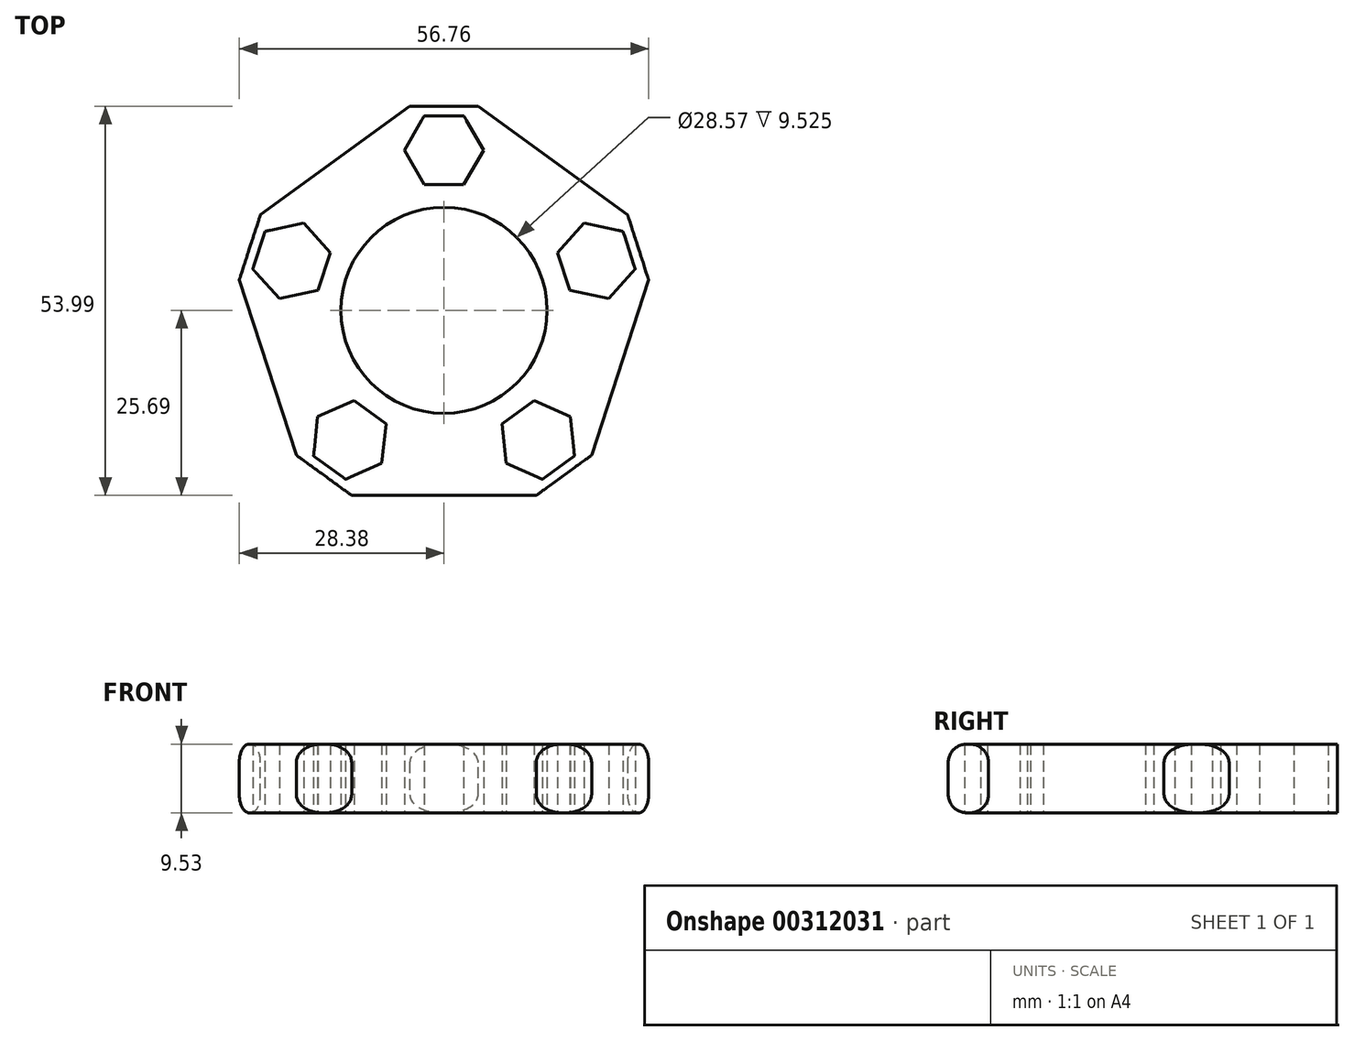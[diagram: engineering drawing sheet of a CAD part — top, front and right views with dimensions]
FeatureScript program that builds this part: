
annotation { "Feature Type Name" : "Feature", "Feature Type Description" : "" }
export const myFeature = defineFeature(function(context is Context, id is Id, definition is map)
    precondition{}
    {
        {
            var Q0;
            Q0=qCreatedBy(makeId("Top.planeOp"),FACE);
            var sketch = newSketch(context, id + "F0", { "sketchPlane" : qUnion([Q0])});
            skCircle(sketch, "E0", {"center": v(0, 0) * mm, "radius": 14.29 * mm});
            skLineSegment(sketch, "E1.0", {"start": v(-2.75, 26.99) * mm, "end": v(2.75, 26.99) * mm});
            skLineSegment(sketch, "E1.1", {"start": v(2.75, 26.99) * mm, "end": v(5.5, 22.23) * mm});
            skLineSegment(sketch, "E1.2", {"start": v(5.5, 22.23) * mm, "end": v(2.75, 17.46) * mm});
            skLineSegment(sketch, "E1.3", {"start": v(2.75, 17.46) * mm, "end": v(-2.75, 17.46) * mm});
            skLineSegment(sketch, "E1.4", {"start": v(-2.75, 17.46) * mm, "end": v(-5.5, 22.22) * mm});
            skLineSegment(sketch, "E1.5", {"start": v(-5.5, 22.22) * mm, "end": v(-2.75, 26.99) * mm});
            skPoint(sketch, "E1.0.midPoint", {"position": v(0, 26.99) * mm});
            skLineSegment(sketch, "E2.1.0", {"start": v(-19.44, 12.1) * mm, "end": v(-15.76, 8.01) * mm});
            skLineSegment(sketch, "E2.1.1", {"start": v(-17.46, 2.78) * mm, "end": v(-22.84, 1.64) * mm});
            skLineSegment(sketch, "E2.1.2", {"start": v(-15.76, 8.01) * mm, "end": v(-17.46, 2.78) * mm});
            skLineSegment(sketch, "E2.1.3", {"start": v(-22.84, 1.64) * mm, "end": v(-26.52, 5.72) * mm});
            skLineSegment(sketch, "E2.1.4", {"start": v(-24.82, 10.95) * mm, "end": v(-19.44, 12.1) * mm});
            skLineSegment(sketch, "E2.1.5", {"start": v(-26.52, 5.72) * mm, "end": v(-24.82, 10.95) * mm});
            skLineSegment(sketch, "E2.2.0", {"start": v(-17.51, -14.75) * mm, "end": v(-12.49, -12.51) * mm});
            skLineSegment(sketch, "E2.2.1", {"start": v(-8.04, -15.74) * mm, "end": v(-8.61, -21.21) * mm});
            skLineSegment(sketch, "E2.2.2", {"start": v(-12.49, -12.51) * mm, "end": v(-8.04, -15.74) * mm});
            skLineSegment(sketch, "E2.2.3", {"start": v(-8.61, -21.21) * mm, "end": v(-13.64, -23.45) * mm});
            skLineSegment(sketch, "E2.2.4", {"start": v(-18.09, -20.22) * mm, "end": v(-17.51, -14.75) * mm});
            skLineSegment(sketch, "E2.2.5", {"start": v(-13.64, -23.45) * mm, "end": v(-18.09, -20.22) * mm});
            skLineSegment(sketch, "E2.3.0", {"start": v(8.61, -21.21) * mm, "end": v(8.04, -15.74) * mm});
            skLineSegment(sketch, "E2.3.1", {"start": v(12.49, -12.51) * mm, "end": v(17.51, -14.75) * mm});
            skLineSegment(sketch, "E2.3.2", {"start": v(8.04, -15.74) * mm, "end": v(12.49, -12.51) * mm});
            skLineSegment(sketch, "E2.3.3", {"start": v(17.51, -14.75) * mm, "end": v(18.09, -20.22) * mm});
            skLineSegment(sketch, "E2.3.4", {"start": v(13.64, -23.45) * mm, "end": v(8.61, -21.21) * mm});
            skLineSegment(sketch, "E2.3.5", {"start": v(18.09, -20.22) * mm, "end": v(13.64, -23.45) * mm});
            skLineSegment(sketch, "E2.4.0", {"start": v(22.84, 1.64) * mm, "end": v(17.46, 2.78) * mm});
            skLineSegment(sketch, "E2.4.1", {"start": v(15.76, 8.01) * mm, "end": v(19.44, 12.1) * mm});
            skLineSegment(sketch, "E2.4.2", {"start": v(17.46, 2.78) * mm, "end": v(15.76, 8.01) * mm});
            skLineSegment(sketch, "E2.4.3", {"start": v(19.44, 12.1) * mm, "end": v(24.82, 10.95) * mm});
            skLineSegment(sketch, "E2.4.4", {"start": v(26.52, 5.72) * mm, "end": v(22.84, 1.64) * mm});
            skLineSegment(sketch, "E2.4.5", {"start": v(24.82, 10.95) * mm, "end": v(26.52, 5.72) * mm});
            skPoint(sketch, "E3.center.orphan", {"position": v(0, 22.23) * mm});
            skLineSegment(sketch, "E4.0", {"start": v(0, 31.75) * mm, "end": v(30.2, 9.81) * mm});
            skLineSegment(sketch, "E4.1", {"start": v(30.2, 9.81) * mm, "end": v(18.66, -25.69) * mm});
            skLineSegment(sketch, "E4.2", {"start": v(18.66, -25.69) * mm, "end": v(-18.66, -25.69) * mm});
            skLineSegment(sketch, "E4.3", {"start": v(-18.66, -25.69) * mm, "end": v(-30.2, 9.81) * mm});
            skLineSegment(sketch, "E4.4", {"start": v(-30.2, 9.81) * mm, "end": v(0, 31.75) * mm});
            skSolve(sketch);
        }
        {
            var Q0;
            Q0=makeQuery(id+"F0.imprint","IMPRINT",FACE,{"disambiguationData":[TD([[makeQuery(id+"F0.imprint","IMPRINT",EDGE,{"derivedFrom":sQuery(id+"F0.wireOp",EDGE,"E0")}),-1.0]])]});
            extrude(context, id + "F1", {"entities" : qUnion([Q0]), "depth" : 9.52 * mm});
        }
        {
            var Q0;
            Q0=makeQuery(id+"F1.opExtrude","SWEPT_EDGE",EDGE,{"disambiguationData":[OSD([sQuery(id+"F0.wireOp",EDGE,"E4.2"),sQuery(id+"F0.wireOp",EDGE,"E4.3")])]});
            var Q1;
            Q1=makeQuery(id+"F1.opExtrude","SWEPT_EDGE",EDGE,{"disambiguationData":[OSD([sQuery(id+"F0.wireOp",EDGE,"E4.1"),sQuery(id+"F0.wireOp",EDGE,"E4.2")])]});
            var Q2;
            Q2=makeQuery(id+"F1.opExtrude","SWEPT_EDGE",EDGE,{"disambiguationData":[OSD([sQuery(id+"F0.wireOp",EDGE,"E4.0"),sQuery(id+"F0.wireOp",EDGE,"E4.1")])]});
            var Q3;
            Q3=makeQuery(id+"F1.opExtrude","SWEPT_EDGE",EDGE,{"disambiguationData":[OSD([sQuery(id+"F0.wireOp",EDGE,"E4.0"),sQuery(id+"F0.wireOp",EDGE,"E4.4")])]});
            var Q4;
            Q4=makeQuery(id+"F1.opExtrude","SWEPT_EDGE",EDGE,{"disambiguationData":[OSD([sQuery(id+"F0.wireOp",EDGE,"E4.3"),sQuery(id+"F0.wireOp",EDGE,"E4.4")])]});
            chamfer(context, id + "F2", {"entities" : qUnion([Q0, Q1, Q2, Q3, Q4]), "width" : 8.08 * mm, "tangentPropagation" : true});
        }
        {
            var Q0;
            Q0=makeQuery(id+"F1.opExtrude","CAP_EDGE",EDGE,{"disambiguationData":[OSD([sQuery(id+"F0.wireOp",EDGE,"E4.1")])],"isStart":false});
            var Q1;
            Q1=makeQuery(id+"F1.opExtrude","CAP_EDGE",EDGE,{"disambiguationData":[OSD([sQuery(id+"F0.wireOp",EDGE,"E4.2")])],"isStart":false});
            var Q2;
            Q2=makeQuery(id+"F1.opExtrude","CAP_EDGE",EDGE,{"disambiguationData":[OSD([sQuery(id+"F0.wireOp",EDGE,"E4.3")])],"isStart":false});
            var Q3;
            Q3=makeQuery(id+"F1.opExtrude","CAP_EDGE",EDGE,{"disambiguationData":[OSD([sQuery(id+"F0.wireOp",EDGE,"E4.4")])],"isStart":false});
            var Q4;
            Q4=makeQuery(id+"F1.opExtrude","CAP_EDGE",EDGE,{"disambiguationData":[OSD([sQuery(id+"F0.wireOp",EDGE,"E4.0")])],"isStart":false});
            fillet(context, id + "F3", {"entities" : qUnion([Q0, Q1, Q2, Q3, Q4]), "radius" : 2.54 * mm, "tangentPropagation" : true, "allowEdgeOverflow" : false});
        }
        {
            var Q0;
            Q0=makeQuery(id+"F1.opExtrude","CAP_EDGE",EDGE,{"disambiguationData":[OSD([sQuery(id+"F0.wireOp",EDGE,"E4.1")])],"isStart":true});
            var Q1;
            Q1=makeQuery(id+"F1.opExtrude","CAP_EDGE",EDGE,{"disambiguationData":[OSD([sQuery(id+"F0.wireOp",EDGE,"E4.2")])],"isStart":true});
            var Q2;
            Q2=makeQuery(id+"F1.opExtrude","CAP_EDGE",EDGE,{"disambiguationData":[OSD([sQuery(id+"F0.wireOp",EDGE,"E4.4")])],"isStart":true});
            var Q3;
            Q3=makeQuery(id+"F1.opExtrude","CAP_EDGE",EDGE,{"disambiguationData":[OSD([sQuery(id+"F0.wireOp",EDGE,"E4.0")])],"isStart":true});
            var Q4;
            Q4=makeQuery(id+"F1.opExtrude","CAP_EDGE",EDGE,{"disambiguationData":[OSD([sQuery(id+"F0.wireOp",EDGE,"E4.3")])],"isStart":true});
            fillet(context, id + "F4", {"entities" : qUnion([Q0, Q1, Q2, Q3, Q4]), "radius" : 2.54 * mm, "tangentPropagation" : true, "allowEdgeOverflow" : false});
        }
    });
